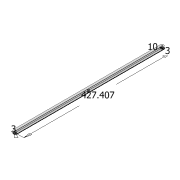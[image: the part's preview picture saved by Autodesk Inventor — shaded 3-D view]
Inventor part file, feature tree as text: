
AUTODESK INVENTOR PART (.ipt)
format: ipt  version: 2022 (Build 260153000, 153)  size: 85,504 bytes
history: native  units: mm
features: extrude x1, sketch x1
ambient origin geometry x8: Origin, YZ Plane, XZ Plane, XY Plane, X Axis, Y Axis, Z Axis, Center Point
bodies: Solid1 (feature_tree)
feature tree (2):
  extrude  "Extrusion1"  Depth=10.0mm
  sketch  "Sketch1"  dims[d1=427.407mm d2=10.0mm d3=3.0mm d4=3.0mm d5=6.0mm d6=0.0mm]
